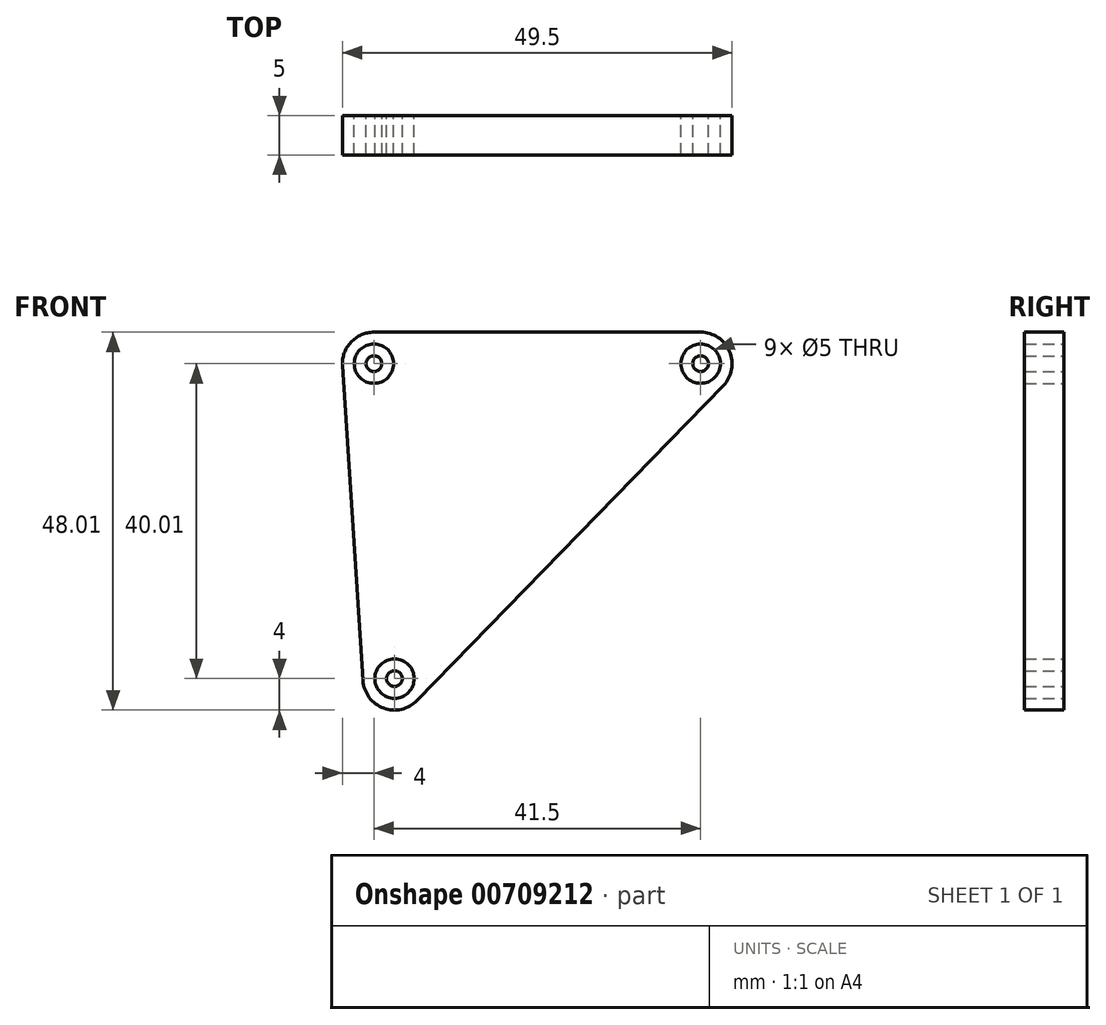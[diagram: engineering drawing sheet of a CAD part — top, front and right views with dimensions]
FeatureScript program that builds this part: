
annotation { "Feature Type Name" : "Feature", "Feature Type Description" : "" }
export const myFeature = defineFeature(function(context is Context, id is Id, definition is map)
    precondition{}
    {
        {
            var Q0;
            Q0=qCreatedBy(makeId("Front.planeOp"),FACE);
            var sketch = newSketch(context, id + "F0", { "sketchPlane" : qUnion([Q0])});
            skArc(sketch, "E0", {"start": v(-15.71, 6.74) * mm, "mid": v(-18.63, 5.47) * mm, "end": v(-19.7, 2.48) * mm});
            skArc(sketch, "E1", {"start": v(28.66, -0.05) * mm, "mid": v(29.47, 4.3) * mm, "end": v(25.79, 6.74) * mm});
            skArc(sketch, "E2", {"start": v(-17.1, -37.53) * mm, "mid": v(-14.48, -41.02) * mm, "end": v(-10.23, -40.06) * mm});
            skLineSegment(sketch, "E3", {"start": v(-19.7, 2.48) * mm, "end": v(-17.1, -37.53) * mm});
            skLineSegment(sketch, "E4", {"start": v(-10.23, -40.06) * mm, "end": v(28.66, -0.05) * mm});
            skLineSegment(sketch, "E5", {"start": v(-15.71, 6.74) * mm, "end": v(25.79, 6.74) * mm});
            skCircle(sketch, "E6", {"center": v(-15.71, 2.74) * mm, "radius": 2.5 * mm});
            skCircle(sketch, "E7", {"center": v(-13.1, -37.27) * mm, "radius": 2.5 * mm});
            skCircle(sketch, "E8", {"center": v(-13.1, -37.27) * mm, "radius": 1 * mm});
            skCircle(sketch, "E9", {"center": v(-15.71, 2.74) * mm, "radius": 1 * mm});
            skCircle(sketch, "E10", {"center": v(25.79, 2.74) * mm, "radius": 2.5 * mm});
            skCircle(sketch, "E11", {"center": v(25.79, 2.74) * mm, "radius": 1 * mm});
            skSolve(sketch);
        }
        {
            var Q0;
            Q0=makeQuery(id+"F0.imprint","IMPRINT",FACE,{"disambiguationData":[TD([[makeQuery(id+"F0.imprint","IMPRINT",EDGE,{"derivedFrom":sQuery(id+"F0.wireOp",EDGE,"E0")}),1.0]])]});
            var Q1;
            Q1=makeQuery(id+"F0.imprint","IMPRINT",FACE,{"disambiguationData":[TD([[makeQuery(id+"F0.imprint","IMPRINT",EDGE,{"derivedFrom":sQuery(id+"F0.wireOp",EDGE,"E9")}),1.0]])]});
            var Q2;
            Q2=makeQuery(id+"F0.imprint","IMPRINT",FACE,{"disambiguationData":[TD([[makeQuery(id+"F0.imprint","IMPRINT",EDGE,{"derivedFrom":sQuery(id+"F0.wireOp",EDGE,"E8")}),1.0]])]});
            var Q3;
            Q3=makeQuery(id+"F0.imprint","IMPRINT",FACE,{"disambiguationData":[TD([[makeQuery(id+"F0.imprint","IMPRINT",EDGE,{"derivedFrom":sQuery(id+"F0.wireOp",EDGE,"E11")}),1.0]])]});
            extrude(context, id + "F1", {"entities" : qUnion([Q0, Q1, Q2, Q3]), "depth" : 5 * mm, "offsetDistance" : 25 * mm});
        }
    });
